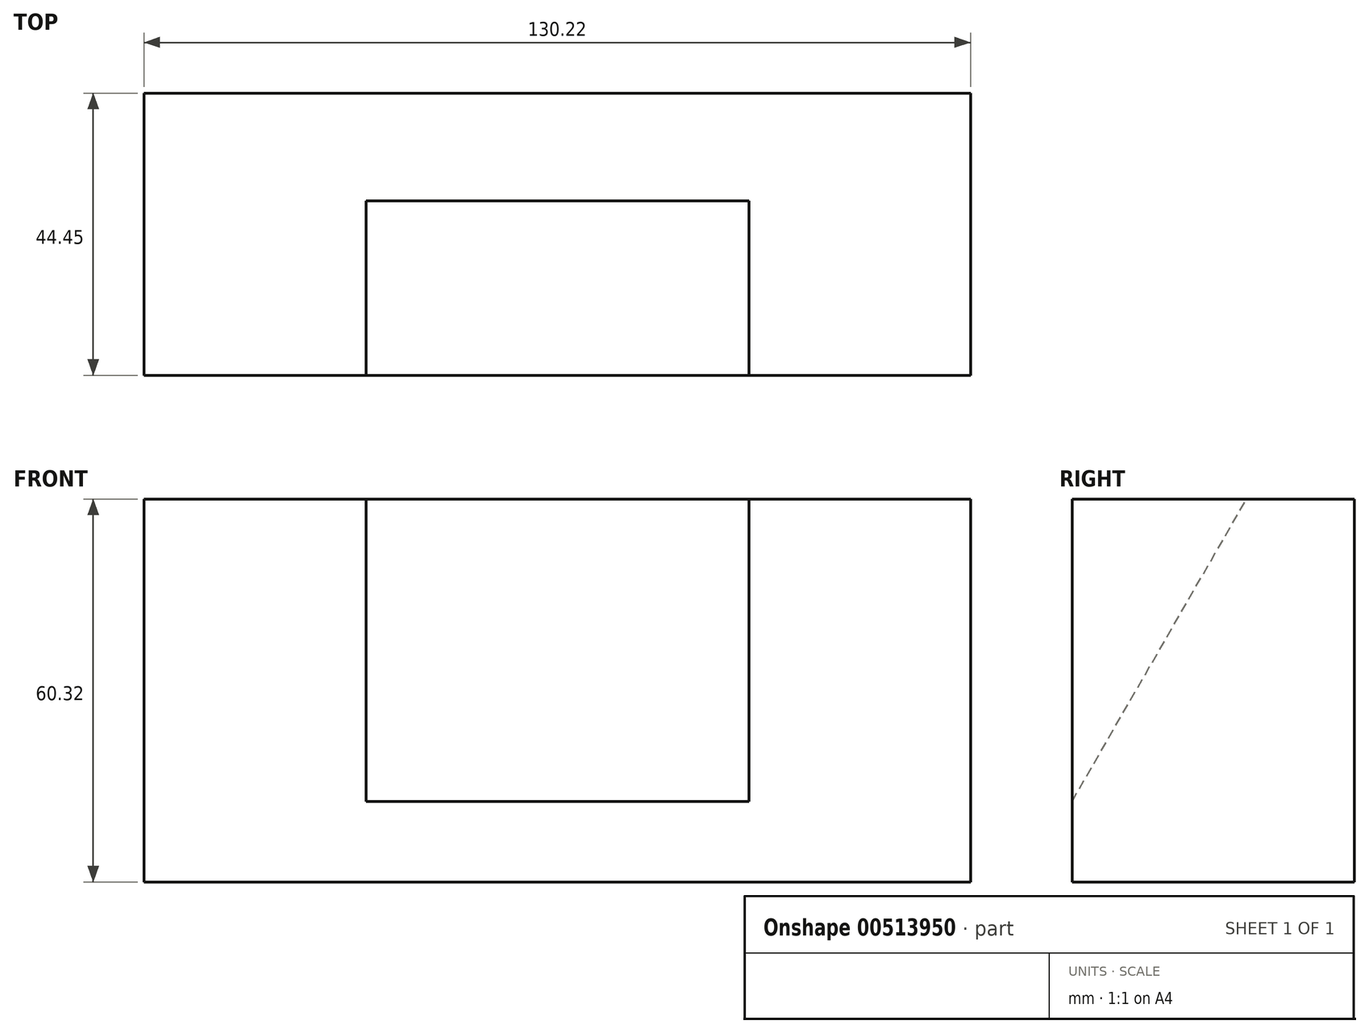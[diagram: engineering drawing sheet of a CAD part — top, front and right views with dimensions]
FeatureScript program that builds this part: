
annotation { "Feature Type Name" : "Feature", "Feature Type Description" : "" }
export const myFeature = defineFeature(function(context is Context, id is Id, definition is map)
    precondition{}
    {
        {
            var Q0;
            Q0=qCreatedBy(makeId("Front.planeOp"),FACE);
            var sketch = newSketch(context, id + "F0", { "sketchPlane" : qUnion([Q0])});
            skLineSegment(sketch, "E0.bottom", {"start": v(-64.07, 23.9) * mm, "end": v(66.1, 23.9) * mm});
            skLineSegment(sketch, "E0.top", {"start": v(-64.07, -36.42) * mm, "end": v(66.1, -36.42) * mm});
            skLineSegment(sketch, "E0.left", {"start": v(-64.07, 23.9) * mm, "end": v(-64.07, -36.42) * mm});
            skLineSegment(sketch, "E0.right", {"start": v(66.1, 23.9) * mm, "end": v(66.1, -36.42) * mm});
            skSolve(sketch);
        }
        {
            var Q0;
            Q0=makeQuery(id+"F0.imprint","IMPRINT",FACE,{"disambiguationData":[TD([[makeQuery(id+"F0.imprint","IMPRINT",EDGE,{"derivedFrom":sQuery(id+"F0.wireOp",EDGE,"E0.bottom")}),-1.0]])]});
            extrude(context, id + "F1", {"entities" : qUnion([Q0]), "depth" : 44.45 * mm, "offsetDistance" : 25.4 * mm});
        }
        {
            var Q0;
            Q0=makeQuery(id+"F1.opExtrude","CAP_FACE",FACE,{"disambiguationData":[OSD([sQuery(id+"F0.wireOp",EDGE,"E0.bottom"),sQuery(id+"F0.wireOp",EDGE,"E0.top"),sQuery(id+"F0.wireOp",EDGE,"E0.left"),sQuery(id+"F0.wireOp",EDGE,"E0.right")])],"isStart":false});
            var sketch = newSketch(context, id + "F2", { "sketchPlane" : qUnion([Q0])});
            skLineSegment(sketch, "E1.bottom", {"start": v(-29.14, 23.9) * mm, "end": v(31.18, 23.9) * mm});
            skLineSegment(sketch, "E1.top", {"start": v(-29.14, -23.72) * mm, "end": v(31.18, -23.72) * mm});
            skLineSegment(sketch, "E1.left", {"start": v(-29.14, 23.9) * mm, "end": v(-29.14, -23.72) * mm});
            skLineSegment(sketch, "E1.right", {"start": v(31.18, 23.9) * mm, "end": v(31.18, -23.72) * mm});
            skSolve(sketch);
        }
        {
            var Q0;
            Q0=makeQuery(id+"F2.imprint","IMPRINT",FACE,{"disambiguationData":[TD([[makeQuery(id+"F2.imprint","IMPRINT",EDGE,{"derivedFrom":sQuery(id+"F2.wireOp",EDGE,"E1.top")}),-1.0]])]});
            var sketch = newSketch(context, id + "F3", { "sketchPlane" : qUnion([Q0])});
            skLineSegment(sketch, "E2.bottom", {"start": v(66.13, -36.33) * mm, "end": v(31.23, -36.33) * mm});
            skLineSegment(sketch, "E2.top", {"start": v(66.13, 24.08) * mm, "end": v(31.23, 24.08) * mm});
            skLineSegment(sketch, "E2.left", {"start": v(66.13, -36.33) * mm, "end": v(66.13, 24.08) * mm});
            skLineSegment(sketch, "E2.right", {"start": v(31.23, -36.33) * mm, "end": v(31.23, 24.08) * mm});
            skSolve(sketch);
        }
        {
            var Q0;
            Q0 = qSketchRegion(id + "F3", true);
            extrude(context, id + "F4", {"entities" : qUnion([Q0]), "operationType" : NewBodyOperationType.REMOVE, "oppositeDirection" : true, "depth" : 44.45 * mm, "offsetDistance" : 25.4 * mm});
        }
        {
            var Q0;
            Q0=makeQuery(id+"F4.boolean.opBoolean","COPY",FACE,{"derivedFrom":makeQuery(id+"F4.opExtrude","SWEPT_FACE",FACE,{"disambiguationData":[OSD([sQuery(id+"F3.wireOp",EDGE,"E2.bottom")])]})});
            extrude(context, id + "F5", {"entities" : qUnion([Q0]), "operationType" : NewBodyOperationType.REMOVE, "oppositeDirection" : true, "depth" : 25.4 * mm, "offsetDistance" : 25.4 * mm});
        }
        {
            var Q0;
            {var subQ0=sQuery(id+"F3.wireOp",EDGE,"E2.right");Q0=makeQuery(id+"F5.boolean.opBoolean","MERGE",FACE,{"derivedFrom":[makeQuery(id+"F4.boolean.opBoolean","COPY",FACE,{"derivedFrom":makeQuery(id+"F4.opExtrude","SWEPT_FACE",FACE,{"disambiguationData":[OSD([subQ0])]})}),makeQuery(id+"F5.opExtrude","SWEPT_FACE",FACE,{"disambiguationData":[OSD([sQuery(id+"F3.wireOp",EDGE,"E2.bottom"),subQ0])]})]});}
            var sketch = newSketch(context, id + "F6", { "sketchPlane" : qUnion([Q0])});
            skLineSegment(sketch, "E3", {"start": v(-44.45, -23.72) * mm, "end": v(-16.95, 23.9) * mm});
            skSolve(sketch);
        }
        {
            var Q0;
            {var subQ0=sQuery(id+"F6.wireOp",EDGE,"E3");Q0=makeQuery(id+"F6.imprint","IMPRINT",FACE,{"disambiguationData":[TD([[makeQuery(id+"F6.imprint","IMPRINT",EDGE,{"derivedFrom":subQ0}),1.0]])]});}
            extrude(context, id + "F7", {"entities" : qUnion([Q0]), "operationType" : NewBodyOperationType.REMOVE, "oppositeDirection" : true, "depth" : 60.32 * mm, "offsetDistance" : 25.4 * mm});
        }
        {
            var Q0;
            {var subQ0=sQuery(id+"F3.wireOp",EDGE,"E2.right");Q0=makeQuery(id+"F5.boolean.opBoolean","MERGE",FACE,{"derivedFrom":[makeQuery(id+"F4.boolean.opBoolean","COPY",FACE,{"derivedFrom":makeQuery(id+"F4.opExtrude","SWEPT_FACE",FACE,{"disambiguationData":[OSD([subQ0])]})}),makeQuery(id+"F5.opExtrude","SWEPT_FACE",FACE,{"disambiguationData":[OSD([sQuery(id+"F3.wireOp",EDGE,"E2.bottom"),subQ0])]})]});}
            var sketch = newSketch(context, id + "F8", { "sketchPlane" : qUnion([Q0])});
            skLineSegment(sketch, "E4.bottom", {"start": v(0, -36.42) * mm, "end": v(-44.45, -36.42) * mm});
            skLineSegment(sketch, "E4.top", {"start": v(0, 23.9) * mm, "end": v(-44.45, 23.9) * mm});
            skLineSegment(sketch, "E4.left", {"start": v(0, -36.42) * mm, "end": v(0, 23.9) * mm});
            skLineSegment(sketch, "E4.right", {"start": v(-44.45, -36.42) * mm, "end": v(-44.45, 23.9) * mm});
            skSolve(sketch);
        }
        {
            var Q0;
            Q0 = qSketchRegion(id + "F8", true);
            extrude(context, id + "F9", {"entities" : qUnion([Q0]), "operationType" : NewBodyOperationType.ADD, "depth" : 34.92 * mm, "offsetDistance" : 25.4 * mm});
        }
    });
